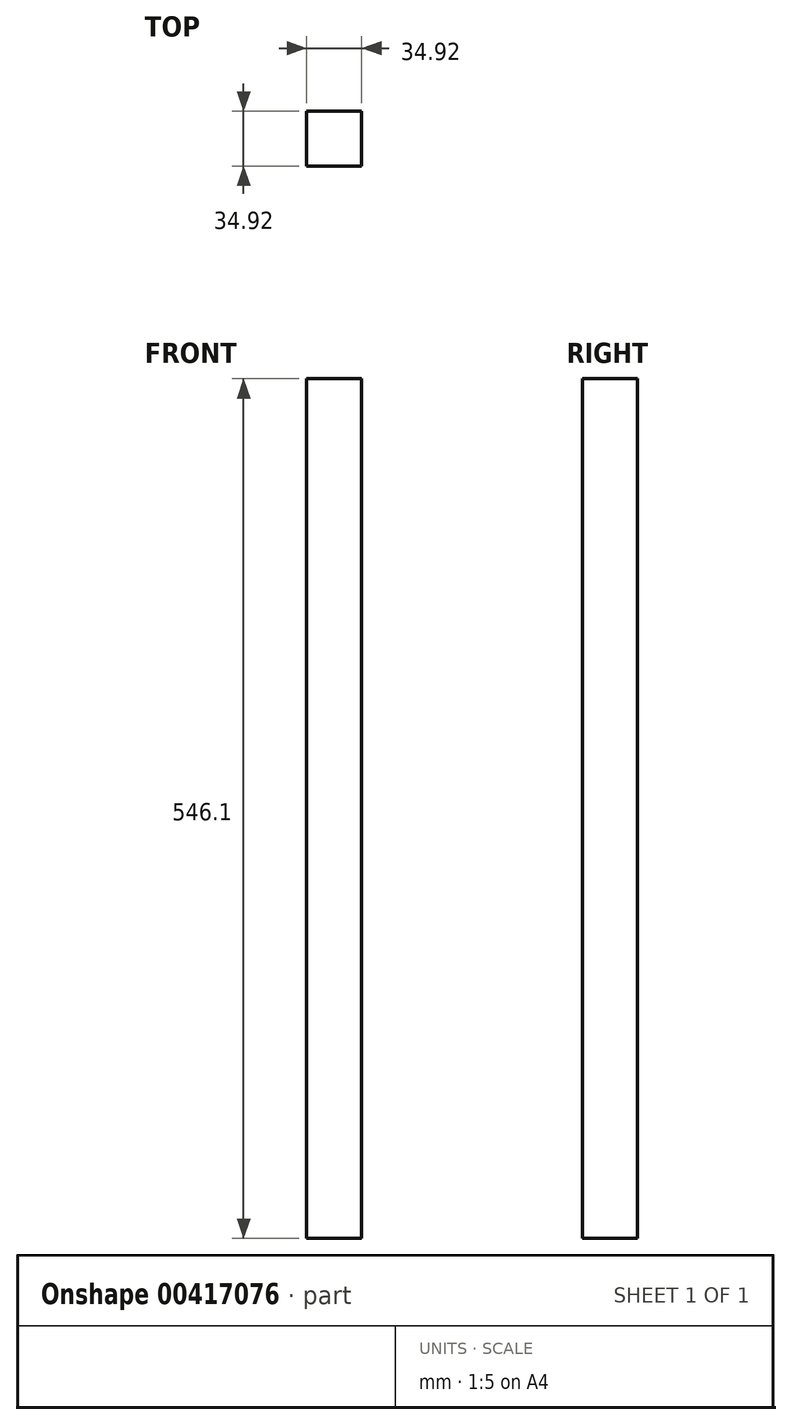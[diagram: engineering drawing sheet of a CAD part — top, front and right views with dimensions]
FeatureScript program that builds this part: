
annotation { "Feature Type Name" : "Feature", "Feature Type Description" : "" }
export const myFeature = defineFeature(function(context is Context, id is Id, definition is map)
    precondition{}
    {
        {
            var Q0;
            Q0=qCreatedBy(makeId("Top.planeOp"),FACE);
            var sketch = newSketch(context, id + "F0", { "sketchPlane" : qUnion([Q0])});
            skLineSegment(sketch, "E0.bottom", {"start": v(17.46, 17.46) * mm, "end": v(-17.46, 17.46) * mm});
            skLineSegment(sketch, "E0.top", {"start": v(17.46, -17.46) * mm, "end": v(-17.46, -17.46) * mm});
            skLineSegment(sketch, "E0.left", {"start": v(17.46, 17.46) * mm, "end": v(17.46, -17.46) * mm});
            skLineSegment(sketch, "E0.right", {"start": v(-17.46, 17.46) * mm, "end": v(-17.46, -17.46) * mm});
            skPoint(sketch, "E0.middle", {"position": v(0, 0) * mm});
            skSolve(sketch);
        }
        {
            var Q0;
            Q0 = qSketchRegion(id + "F0", true);
            extrude(context, id + "F1", {"entities" : qUnion([Q0]), "depth" : 546.1 * mm});
        }
    });
